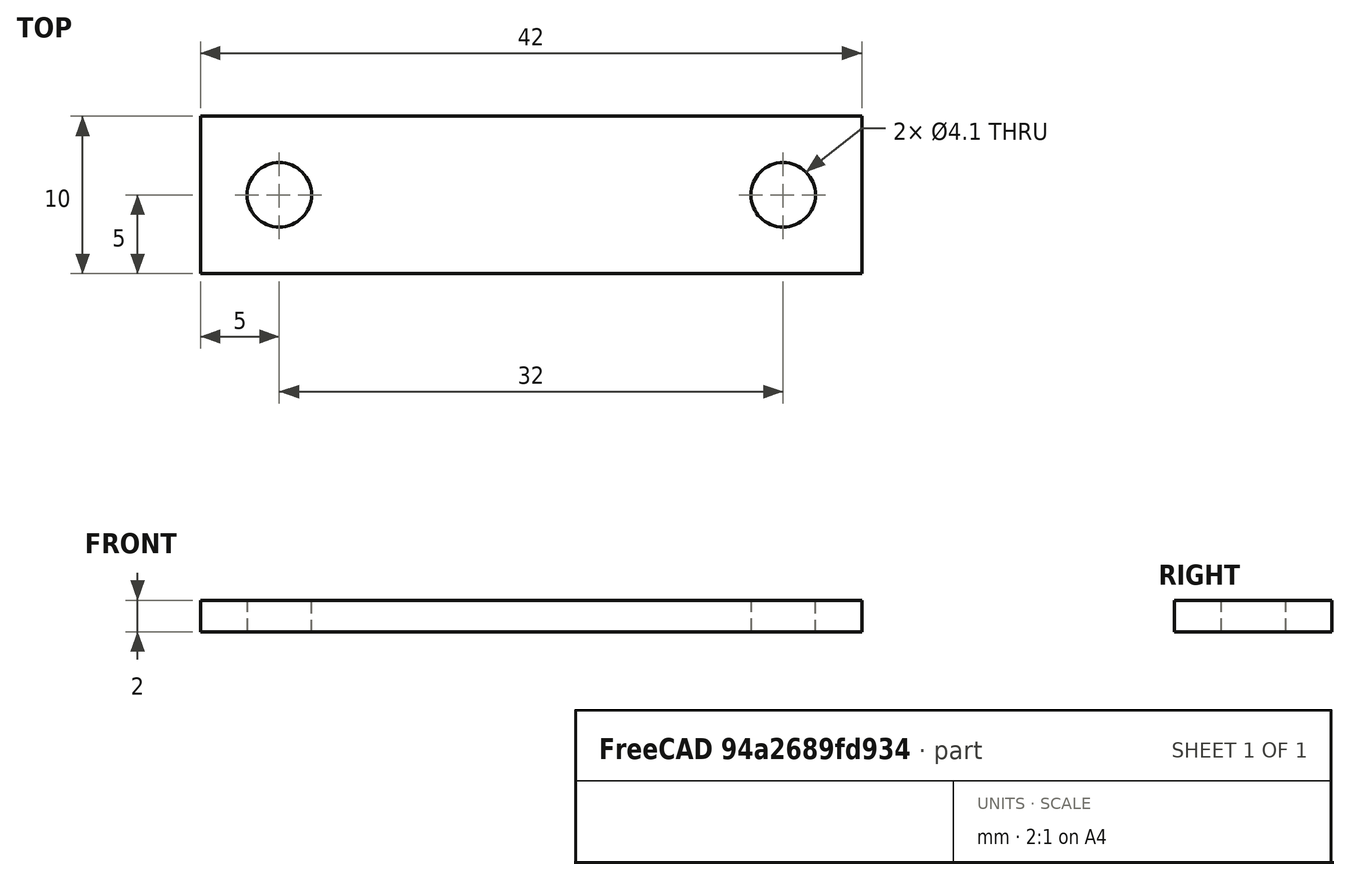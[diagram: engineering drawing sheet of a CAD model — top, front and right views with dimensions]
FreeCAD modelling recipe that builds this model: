
FCSTD DOCUMENT  (FreeCAD 1.0R38806 (Git))
Label: Frame75Parts
License: All rights reserved
LicenseURL: https://en.wikipedia.org/wiki/All_rights_reserved
objects: PartDesign::Plane×1, Sketcher::SketchObject×1, PartDesign::Pad×1, PartDesign::Body×1
note: 7 computed .brp shape members not serialized (recipe doc carries the construction recipe); baked Part::Feature solids carry a one-line shape summary decoded from their .brp

FEATURE [PartDesign::Plane] DatumPlane001  label="DatumPlane"
  AttachmentSupport = -> [XY_Plane001]
  Length = 89.4097
  MapMode = 5
  ResizeMode = 0
  Width = 62.4097
FEATURE [Sketcher::SketchObject] Sketch004  label="SensorCoverS"
  ArcFitTolerance = 0
  AttachmentSupport = -> [DatumPlane001]
  FullyConstrained = true
  MakeInternals = false
  MapMode = 5
  sketch-geometry (6):
    g0: LineSegment StartX=10 StartY=20 StartZ=0 EndX=10 EndY=10 EndZ=0
    g1: LineSegment StartX=10 StartY=10 StartZ=0 EndX=52 EndY=10 EndZ=0
    g2: LineSegment StartX=52 StartY=10 StartZ=0 EndX=52 EndY=20 EndZ=0
    g3: LineSegment StartX=52 StartY=20 StartZ=0 EndX=10 EndY=20 EndZ=0
    g4: Circle CenterX=15 CenterY=15 CenterZ=0 NormalX=0 NormalY=0 NormalZ=1 AngleXU=0 Radius=2.05
    g5: Circle CenterX=47 CenterY=15 CenterZ=0 NormalX=0 NormalY=0 NormalZ=1 AngleXU=0 Radius=2.05
  constraints (18):
    c: Vertical(g0)
    c: Coincident(g0,g1)
    c: Horizontal(g1)
    c: Coincident(g1,g2)
    c: Vertical(g2)
    c: Coincident(g2,g3)
    c: Horizontal(g3)
    c: DistanceY(g2,g2) = 10
    c: Equal(g4,g5)
    c: Diameter(g4) = 4.1
    c: DistanceX(g4,g5) = 32
    c: Distance(g4,g1) = 5
    c: Distance(g5,g1) = 5
    c: Coincident(g3,g0)
    c: Distance(g4,g0) = 5
    c: Distance(g5,g2) = 5
    c: DistanceX(g0,g-1) = -10
    c: DistanceY(g0,g-1) = -10
FEATURE [PartDesign::Pad] Pad002  label="SensorCover001"
  Direction = (0,0,1)
  Length = 2
  Length2 = 10
  Profile = -> Sketch004
  ReferenceAxis = -> Sketch004 [N_Axis]
  Suppressed = false
  Type = 0
FEATURE [PartDesign::Body] Body001  label="SensorCover"
  AllowCompound = false
  Group = -> [DatumPlane001,Sketch004,Pad002]
  Origin = -> Origin001
  Tip = -> Pad002
